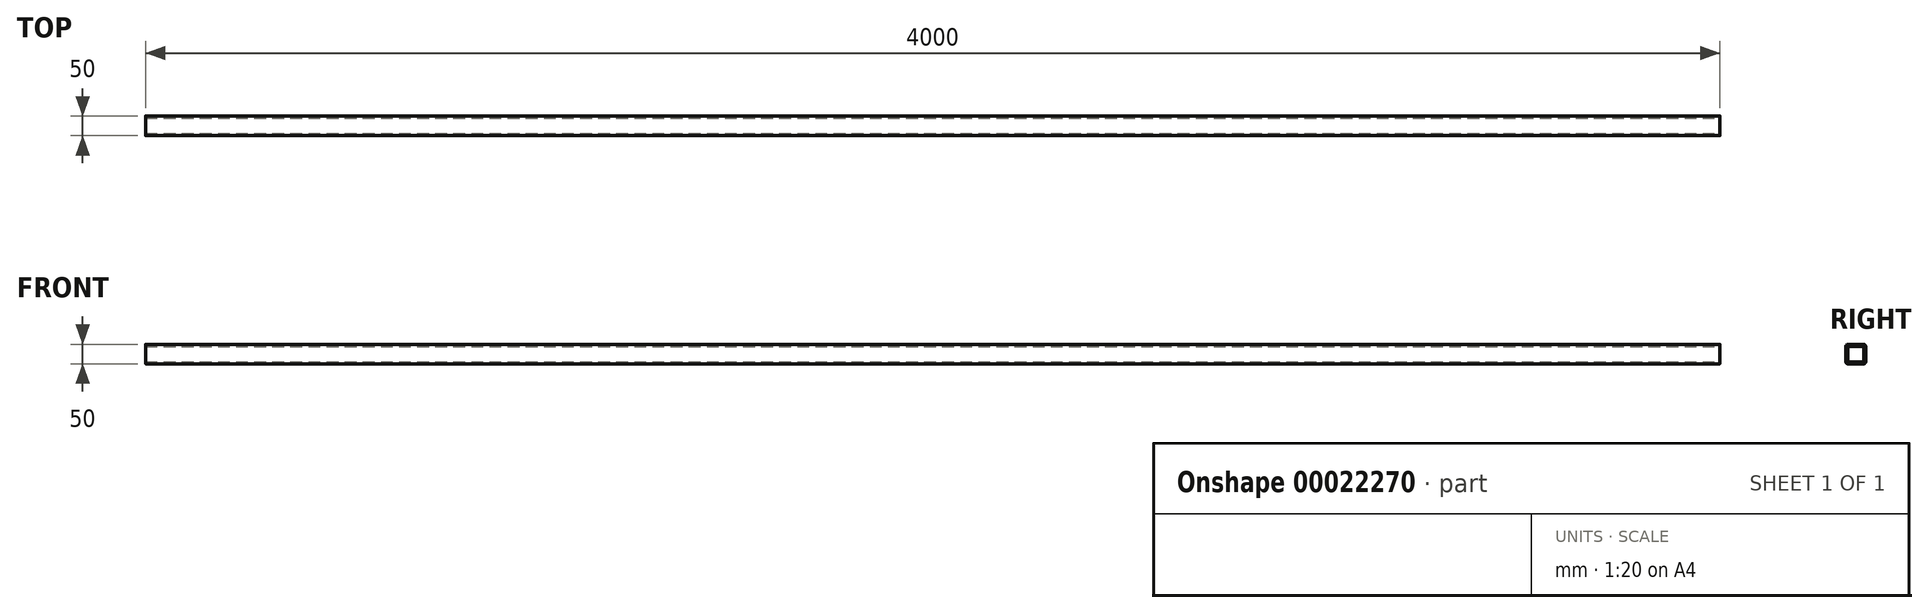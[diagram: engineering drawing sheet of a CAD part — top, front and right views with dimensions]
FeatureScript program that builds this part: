
annotation { "Feature Type Name" : "Feature", "Feature Type Description" : "" }
export const myFeature = defineFeature(function(context is Context, id is Id, definition is map)
    precondition{}
    {
        {
            var Q0;
            Q0=qCreatedBy(makeId("Right.planeOp"),FACE);
            var sketch = newSketch(context, id + "F0", { "sketchPlane" : qUnion([Q0])});
            skLineSegment(sketch, "E0.rect.bottom", {"start": v(20, 25) * mm, "end": v(-20, 25) * mm});
            skLineSegment(sketch, "E0.rect.top", {"start": v(20, -25) * mm, "end": v(-20, -25) * mm});
            skLineSegment(sketch, "E0.rect.left", {"start": v(25, 20) * mm, "end": v(25, -20) * mm});
            skLineSegment(sketch, "E0.rect.right", {"start": v(-25, 20) * mm, "end": v(-25, -20) * mm});
            skPoint(sketch, "E0.rect.middle", {"position": v(0, 0) * mm});
            skPoint(sketch, "E1.visualSharp", {"position": v(25, 25) * mm});
            skArc(sketch, "E1.filletArc", {"start": v(25, 20) * mm, "mid": v(23.54, 23.54) * mm, "end": v(20, 25) * mm});
            skPoint(sketch, "E2.visualSharp", {"position": v(-25, -25) * mm});
            skArc(sketch, "E2.filletArc", {"start": v(-25, -20) * mm, "mid": v(-23.54, -23.54) * mm, "end": v(-20, -25) * mm});
            skPoint(sketch, "E3.visualSharp", {"position": v(25, -25) * mm});
            skArc(sketch, "E3.filletArc", {"start": v(20, -25) * mm, "mid": v(23.54, -23.54) * mm, "end": v(25, -20) * mm});
            skPoint(sketch, "E4.visualSharp", {"position": v(-25, 25) * mm});
            skArc(sketch, "E4.filletArc", {"start": v(-20, 25) * mm, "mid": v(-23.54, 23.54) * mm, "end": v(-25, 20) * mm});
            skLineSegment(sketch, "E5.0", {"start": v(20, 17.5) * mm, "end": v(20, -17.5) * mm});
            skLineSegment(sketch, "E6.0", {"start": v(17.5, 20) * mm, "end": v(-17.5, 20) * mm});
            skLineSegment(sketch, "E7.0", {"start": v(17.5, -20) * mm, "end": v(-17.5, -20) * mm});
            skLineSegment(sketch, "E8.0", {"start": v(-20, 17.5) * mm, "end": v(-20, -17.5) * mm});
            skArc(sketch, "E9.filletArc", {"start": v(-17.5, 20) * mm, "mid": v(-19.27, 19.27) * mm, "end": v(-20, 17.5) * mm});
            skArc(sketch, "E10.filletArc", {"start": v(20, 17.5) * mm, "mid": v(19.27, 19.27) * mm, "end": v(17.5, 20) * mm});
            skArc(sketch, "E11.filletArc", {"start": v(17.5, -20) * mm, "mid": v(19.27, -19.27) * mm, "end": v(20, -17.5) * mm});
            skArc(sketch, "E12.filletArc", {"start": v(-20, -17.5) * mm, "mid": v(-19.27, -19.27) * mm, "end": v(-17.5, -20) * mm});
            skSolve(sketch);
        }
        {
            var Q0;
            Q0=sQuery(id+"F0.wireOp",EDGE,"E7.0");
            var Q1;
            Q1=sQuery(id+"F0.wireOp",EDGE,"E11.filletArc");
            var Q2;
            Q2=sQuery(id+"F0.wireOp",EDGE,"E1.filletArc");
            var Q3;
            Q3=sQuery(id+"F0.wireOp",EDGE,"E0.rect.top");
            var Q4;
            Q4=sQuery(id+"F0.wireOp",EDGE,"E0.rect.right");
            var Q5;
            Q5=sQuery(id+"F0.wireOp",EDGE,"E9.filletArc");
            var Q6;
            Q6=sQuery(id+"F0.wireOp",EDGE,"E10.filletArc");
            var Q7;
            Q7=sQuery(id+"F0.wireOp",EDGE,"E8.0");
            var Q8;
            Q8=sQuery(id+"F0.wireOp",EDGE,"E12.filletArc");
            var Q9;
            Q9=sQuery(id+"F0.wireOp",EDGE,"E6.0");
            var Q10;
            Q10=sQuery(id+"F0.wireOp",EDGE,"E3.filletArc");
            var Q11;
            Q11=sQuery(id+"F0.wireOp",EDGE,"E0.rect.bottom");
            var Q12;
            Q12=sQuery(id+"F0.wireOp",EDGE,"E4.filletArc");
            var Q13;
            Q13=sQuery(id+"F0.wireOp",EDGE,"E5.0");
            var Q14;
            Q14=sQuery(id+"F0.wireOp",EDGE,"E2.filletArc");
            var Q15;
            Q15=sQuery(id+"F0.wireOp",EDGE,"E0.rect.left");
            extrude(context, id + "F1", {"bodyType" : ToolBodyType.SURFACE, "surfaceEntities" : qUnion([Q0, Q1, Q2, Q3, Q4, Q5, Q6, Q7, Q8, Q9, Q10, Q11, Q12, Q13, Q14, Q15]), "depth" : 4000 * mm});
        }
    });
